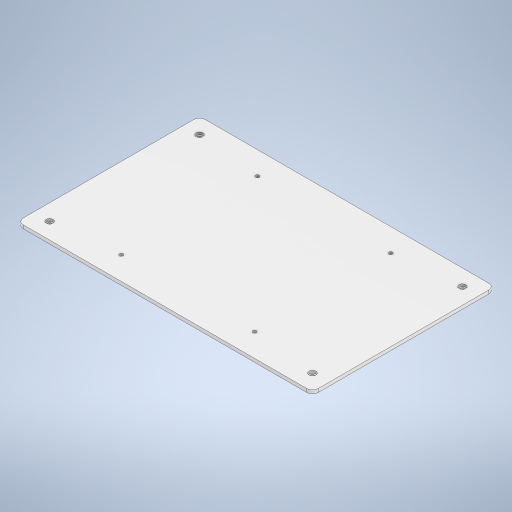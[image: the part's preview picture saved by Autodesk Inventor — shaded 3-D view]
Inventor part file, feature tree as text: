
AUTODESK INVENTOR PART (.ipt)
format: ipt  version: 2024.3 (Build 283343000, 343)  size: 317,952 bytes
history: native  units: mm
features: sketch x6, extrude x3, hole x2, projected_geometry x2, other x1, fillet x1
ambient origin geometry x8: Origin, YZ Plane, XZ Plane, XY Plane, X Axis, Y Axis, Z Axis, Center Point
bodies: Body1 (feature_tree)
feature tree (15):
  other  "ソリッド1"
  extrude  "押し出し1"  Depth=260.0mm
  hole  "穴1"  [1 undecoded]
  extrude  "押し出し4"  Depth=3.0mm TaperAngle=0.0deg
  fillet  "フィレット1"  Radius=30.0mm
  extrude  "押し出し5"  Depth=30.0mm
  hole  "穴2"  [1 undecoded]
  sketch  "スケッチ3"
  sketch  "スケッチ1"
  sketch  "スケッチ7"
  sketch  "スケッチ8"
  projected_geometry  "投影ループ1"
  sketch  "スケッチ9"
  projected_geometry  "投影ループ2"
  sketch  "スケッチ10"
note: 2 required parameter values undecoded (feature->parameter linkage not recoverable at this tier; creation-order binding heuristic only, values carry confidence <= 0.55)
